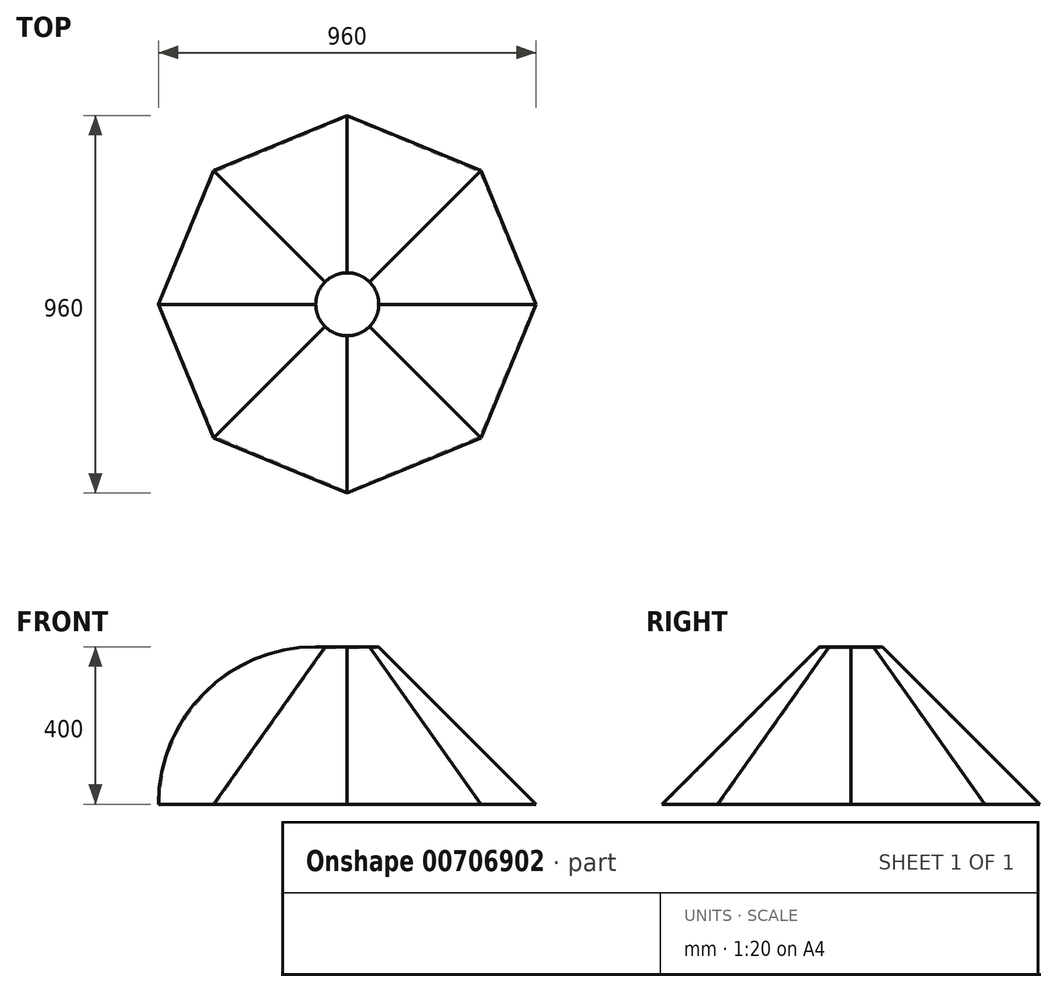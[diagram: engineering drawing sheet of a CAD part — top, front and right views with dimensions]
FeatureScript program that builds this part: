
annotation { "Feature Type Name" : "Feature", "Feature Type Description" : "" }
export const myFeature = defineFeature(function(context is Context, id is Id, definition is map)
    precondition{}
    {
        {
            var Q0;
            Q0=qCreatedBy(makeId("Top.planeOp"),FACE);
            cPlane(context, id + "F0", {"entities" : qUnion([Q0]), "cplaneType" : CPlaneType.OFFSET, "offset" : 400 * mm, "width" : 150 * mm, "height" : 150 * mm});
        }
        {
            var Q0;
            Q0=qCreatedBy(id+"F0.planeOp",FACE);
            var sketch = newSketch(context, id + "F1", { "sketchPlane" : qUnion([Q0])});
            skCircle(sketch, "E0", {"center": v(0, 0) * mm, "radius": 80 * mm});
            skSolve(sketch);
        }
        {
            var Q0;
            Q0=qCreatedBy(makeId("Top.planeOp"),FACE);
            var sketch = newSketch(context, id + "F2", { "sketchPlane" : qUnion([Q0])});
            skCircle(sketch, "E1", {"center": v(0, 0) * mm, "radius": 443.46 * mm});
            skCircle(sketch, "E2.cCircle", {"center": v(0, 0) * mm, "radius": 443.46 * mm, "construction": true});
            skLineSegment(sketch, "E2.0", {"start": v(0, 480) * mm, "end": v(339.41, 339.41) * mm});
            skLineSegment(sketch, "E2.1", {"start": v(339.41, 339.41) * mm, "end": v(480, 0) * mm});
            skLineSegment(sketch, "E2.2", {"start": v(480, 0) * mm, "end": v(339.41, -339.41) * mm});
            skLineSegment(sketch, "E2.3", {"start": v(339.41, -339.41) * mm, "end": v(0, -480) * mm});
            skLineSegment(sketch, "E2.4", {"start": v(0, -480) * mm, "end": v(-339.41, -339.41) * mm});
            skLineSegment(sketch, "E2.5", {"start": v(-339.41, -339.41) * mm, "end": v(-480, 0) * mm});
            skLineSegment(sketch, "E2.6", {"start": v(-480, 0) * mm, "end": v(-339.41, 339.41) * mm});
            skLineSegment(sketch, "E2.7", {"start": v(-339.41, 339.41) * mm, "end": v(0, 480) * mm});
            skPoint(sketch, "E2.0.midPoint", {"position": v(169.7, 409.7) * mm});
            skSolve(sketch);
        }
        {
            var Q0;
            Q0=qCreatedBy(makeId("Front.planeOp"),FACE);
            var sketch = newSketch(context, id + "F3", { "sketchPlane" : qUnion([Q0])});
            skLineSegment(sketch, "E3", {"start": v(0, 0) * mm, "end": v(0, 500) * mm});
            skArc(sketch, "E4", {"start": v(-80, 400) * mm, "mid": v(-362.84, 282.84) * mm, "end": v(-480, 0) * mm});
            skPoint(sketch, "E5.endSnap0", {"position": v(-480, 0) * mm});
            skPoint(sketch, "E6.orphan", {"position": v(-719.96, 0) * mm});
            skSolve(sketch);
        }
        {
            var Q0;
            Q0=makeQuery(id+"F1.imprint","IMPRINT",FACE,{"disambiguationData":[TD([[makeQuery(id+"F1.imprint","IMPRINT",EDGE,{"derivedFrom":sQuery(id+"F1.wireOp",EDGE,"E0")}),1.0]])]});
            var Q1;
            Q1 = qSketchRegion(id + "F2", true);
            var Q2;
            Q2=sQuery(id+"FihstRRLPFOyloX_0.3.F3.wireOp",EDGE,"nV7fds50-S5yT-E7QT-J2T2-OYsLmwIyiznZ");
            var Q3;
            Q3=sQuery(id+"F3.wireOp",EDGE,"E4");
            var Q4;
            Q4=sQuery(id+"FihstRRLPFOyloX_0.1.F3.wireOp",EDGE,"E4");
            var Q5;
            Q5=sQuery(id+"FihstRRLPFOyloX_0.2.F3.wireOp",EDGE,"E4");
            var Q6;
            Q6=sQuery(id+"FihstRRLPFOyloX_0.3.F3.wireOp",EDGE,"E4");
            var Q7;
            Q7=sQuery(id+"FihstRRLPFOyloX_0.4.F3.wireOp",EDGE,"E4");
            var Q8;
            Q8=sQuery(id+"FihstRRLPFOyloX_0.5.F3.wireOp",EDGE,"E4");
            var Q9;
            Q9=sQuery(id+"FihstRRLPFOyloX_0.6.F3.wireOp",EDGE,"E4");
            var Q10;
            Q10=sQuery(id+"FihstRRLPFOyloX_0.7.F3.wireOp",EDGE,"E4");
            loft(context, id + "F4", {"addGuides" : true, "sheetProfilesArray" : [{ "sheetProfileEntities" : qUnion([Q0]) }, { "sheetProfileEntities" : qUnion([Q1]) }], "wireProfilesArray" : [{ "wireProfileEntities" : qUnion([Q2]) }], "guidesArray" : [{ "guideEntities" : qUnion([Q3]), "guideDerivativeType" : LoftGuideDerivativeType.DEFAULT, "guideDerivativeMagnitude" : 1 }, { "guideEntities" : qUnion([Q4]), "guideDerivativeType" : LoftGuideDerivativeType.DEFAULT, "guideDerivativeMagnitude" : 1 }, { "guideEntities" : qUnion([Q5]), "guideDerivativeType" : LoftGuideDerivativeType.DEFAULT, "guideDerivativeMagnitude" : 1 }, { "guideEntities" : qUnion([Q6]), "guideDerivativeType" : LoftGuideDerivativeType.DEFAULT, "guideDerivativeMagnitude" : 1 }, { "guideEntities" : qUnion([Q7]), "guideDerivativeType" : LoftGuideDerivativeType.DEFAULT, "guideDerivativeMagnitude" : 1 }, { "guideEntities" : qUnion([Q8]), "guideDerivativeType" : LoftGuideDerivativeType.DEFAULT, "guideDerivativeMagnitude" : 1 }, { "guideEntities" : qUnion([Q9]), "guideDerivativeType" : LoftGuideDerivativeType.DEFAULT, "guideDerivativeMagnitude" : 1 }, { "guideEntities" : qUnion([Q10]), "guideDerivativeType" : LoftGuideDerivativeType.DEFAULT, "guideDerivativeMagnitude" : 1 }]});
        }
        {
            var Q0;
            {var subQ0=sQuery(id+"F2.wireOp",EDGE,"E1");var subQ4=makeQuery(id+"F2.imprint","INTERSECT",VERTEX,{"derivedFrom":[subQ0,sQuery(id+"F2.wireOp",EDGE,"E2.0")]});Q0=makeQuery(id+"F4.opLoft","CAP_FACE",FACE,{"disambiguationData":[OSD([makeQuery(id+"F2.imprint","IMPRINT",FACE,{"disambiguationData":[TD([[makeQuery(id+"F2.imprint","IMPRINT",EDGE,{"disambiguationData":[TD([[subQ4,1.0]])],"derivedFrom":subQ0}),1.0]])]})])],"isStart":true});}
            shell(context, id + "F5", {"entities" : qUnion([Q0]), "thickness" : 2.5 * mm});
        }
    });
